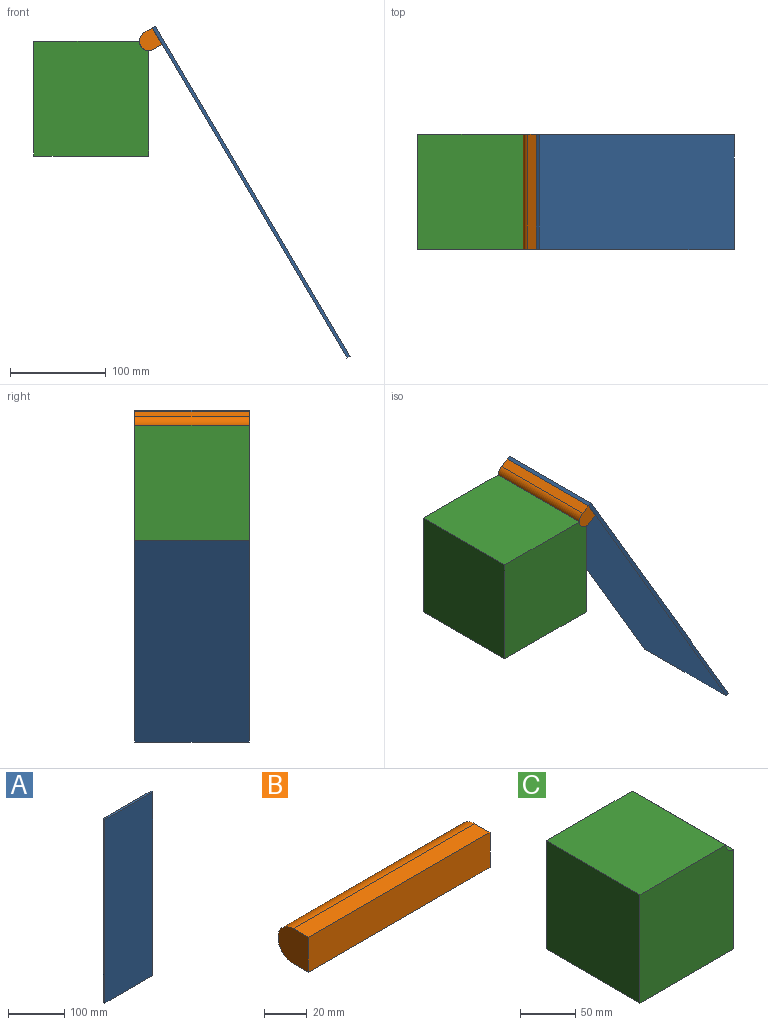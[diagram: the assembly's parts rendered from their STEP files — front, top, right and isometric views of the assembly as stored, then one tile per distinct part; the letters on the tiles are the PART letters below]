
ASSEMBLY  parts=3 mates=2
PART A: 6 faces, bbox 120x4x400 mm
  f0: plane 400x4mm, normal (1,0,0), area 1600mm2, adj f1,f3,f4,f5
  f1: plane 120x4mm, normal (0,0,1), area 480mm2, adj f0,f2,f4,f5
  f2: plane 400x4mm, normal (-1,0,0), area 1600mm2, adj f1,f3,f4,f5
  f3: plane 120x4mm, normal (0,0,-1), area 480mm2, adj f0,f2,f4,f5
  f4: plane 400x120mm, normal (0,1,0), area 48000mm2, adj f0,f1,f2,f3
  f5: plane 400x120mm, normal (0,-1,0), area 48000mm2, adj f0,f1,f2,f3
PART B: 6 faces, bbox 120x20x20 mm
  f0: plane 20x20mm, normal (1,0,0), area 357.1mm2, adj f2,f3,f4,f5
  f1: plane 20x20mm, normal (-1,0,0), area 357.1mm2, adj f2,f3,f4,f5
  f2: plane 120x10mm, normal (0,0,1), area 1200mm2, adj f0,f1,f4,f5
  f3: plane 120x10mm, normal (0,0,-1), area 1200mm2, adj f0,f1,f4,f5
  f4: plane 120x20mm, normal (0,-1,0), area 2400mm2, adj f0,f1,f2,f3
  f5: cylinder r=10mm len=120mm, axis (-1,0,0), area 3769.9mm2, adj f0,f1,f2,f3
PART C: 7 faces, bbox 120x120x120 mm
  f0: plane 120x110mm, normal (1,0,0), area 13200mm2, adj f1,f4,f5,f6
  f1: cylinder r=10mm len=120mm, axis (0,1,0), area 1885mm2, adj f0,f2,f5,f6
  f2: plane 120x110mm, normal (0,0,1), area 13200mm2, adj f1,f3,f5,f6
  f3: plane 120x120mm, normal (-1,0,0), area 14400mm2, adj f2,f4,f5,f6
  f4: plane 120x120mm, normal (0,0,-1), area 14400mm2, adj f0,f3,f5,f6
  f5: plane 120x120mm, normal (0,-1,0), area 14321.5mm2, adj f0,f1,f2,f3,f4
  f6: plane 120x120mm, normal (0,1,0), area 14321.5mm2, adj f0,f1,f2,f3,f4
PLACE A rot(axis=(-0.25,-0.25,0.93),94deg) t=(168.59,0,-96.54)mm
PLACE B rot(axis=(-0.25,-0.25,0.93),94deg) t=(168.59,0,-96.54)mm
PLACE C at identity fixed
MATE revolute C.f1 <-> B.f5  axis (0,1,0) through (60,0,60)mm
MATE fastened A.f4 <-> B.f4  axis (-0.86,0,-0.51) through (63.53,0,73.69)mm
